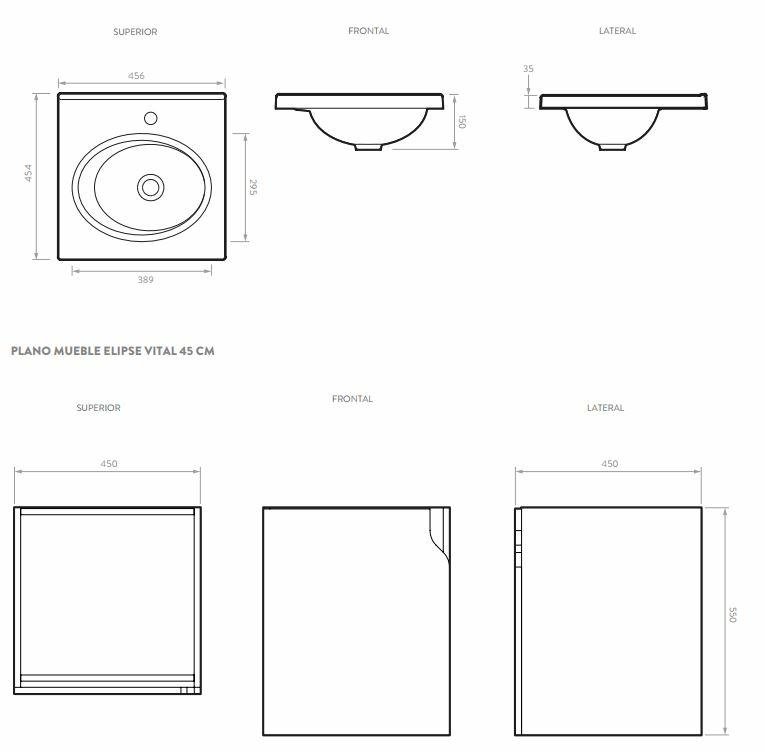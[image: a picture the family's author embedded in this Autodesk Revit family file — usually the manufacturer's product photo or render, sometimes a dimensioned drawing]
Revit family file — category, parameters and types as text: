
# Revit family: LM0036611_Mueble Elipse Vital 60 cm con Lavamanos
name_source: partatom
category: Plumbing Fixtures
units: mm (PartAtom-declared; Revit-internal decimal feet)

## family parameters
Always vertical = Yes
Cut with Voids When Loaded = No
OmniClass Number = 23.45.05.14.14
OmniClass Title = Sinks/Lavatories
Part Type = Normal
Room Calculation Point = No
Round Connector Dimension = Use Diameter
Shared = No
Work Plane-Based = No

## types (2) — shared parameters
Alto = 850 mm  [stored 2.78871 ft]
Ancho = 606 mm
Description = La línea de muebles Elipse Vital compacto que se se adapta a la gran
mayoría de espacios disponibles
diseño y funcionalidad, ALUVIA se inspira en el movimiento y caída del agua en la
naturaleza, es por ello de sus formas orgánicas donde podemos obtener un producto
compacto y de líneas fluidas, que se adapta en espacios pequeños.
el pricipal benefico de los muebles de esta linea es ser un producto compacto que cuenta
con cajón y repisa brindándole al consumidor mayor capacidad de almacenamiento, como
una excelente solución para aquellos espacios pequeños.
Dimensiones Generales (H * W * P) = 21,65” x 23,62” x 17,72” (550,0 x 600 x 450 mm)
Garantia Madera = 5 años
Manufacturer = Corona
Material Lavamanos = Corona_Cerámica_Sinterizada
Peso Bruto aprox = 28,4 lb (12,9 kg)
Peso Neto aprox = 26,9 lb (12,2 kg)
Profundidad = 435 mm
Referencia = LM0036611
Resistencia a la humedad = 8%
Resistencia al rayado = 700 ciclos

## per-type parameters (varying)
| type | Canto | Carga máxima | Densidad | Garantia Herrajes | Material | Model | URL |
| Ref. 604281711 Mueble Aluvia Miel Con Lavamanos |  |  |  |  | Corona_Madera_Carbon |  | https://corona.co |
| Ref. 604286091 Mueble Aluvia Habano Con Lavamanos | PVC rígido 2 mm de calibre. | 99,2 lb (45 kg). | 15 mms 670 kg./m^3. | 1 año | <By Category> | Mueble aluvia miel LVM 45X45 |  |

note: [stored X ft] marks values corroborated as IEEE doubles in the binary element streams (Revit-internal decimal feet)

## geometry (parser evidence)
native form markers: Sweep x28
no freeform markers — native parametric forms only
